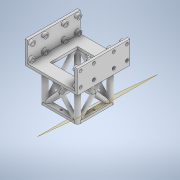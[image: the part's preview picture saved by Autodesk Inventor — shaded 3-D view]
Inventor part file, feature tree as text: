
AUTODESK INVENTOR PART (.ipt)
format: ipt  version: 2022 (Build 260153000, 153)  size: 368,128 bytes
history: native  units: in
note: dims shown in document units (in); Inventor stores cm internally (conversion verified against a paired STEP export)
features: extrude x9, sketch x9, mirror x2, pattern_circular x2, plane x1
ambient origin geometry x8: Origin, YZ Plane, XZ Plane, XY Plane, X Axis, Y Axis, Z Axis, Center Point
bodies: Solid1 (feature_tree)
feature tree (23):
  extrude  "Extrusion1"  Depth=4.0551in
  extrude  "Extrusion2"  Depth=0.1969in
  extrude  "Extrusion3"  Depth=1.5748in TaperAngle=0.0deg
  extrude  "Extrusion4"  Depth=0.3937in
  mirror  "Mirror1"
  extrude  "Extrusion5"  Depth=0.3937in
  extrude  "Extrusion6"  Depth=0.3937in
  extrude  "Extrusion7"  Depth=0.3937in
  extrude  "Extrusion8"  Depth=0.2362in
  pattern_circular  "Circular Pattern1"  [2 undecoded]
  plane  "Work Plane1"
  extrude  "Extrusion9"  Depth=0.3937in
  mirror  "Mirror2"
  pattern_circular  "Circular Pattern2"  [2 undecoded]
  sketch  "Sketch1"  dims[d0=4.0551in d1=4.0551in]
  sketch  "Sketch2"  dims[d2=0.1969in d3=0.0in d4=0.1969in]
  sketch  "Sketch3"  dims[d5=0.1969in d6=1.5748in d7=0.0in]
  sketch  "Sketch4"  dims[d8=0.3937in d9=0.3937in]
  sketch  "Sketch5"  dims[d10=0.3937in d11=0.3937in]
  sketch  "Sketch6"  dims[d12=0.3937in d13=0.3937in]
  sketch  "Sketch7"  dims[d14=0.3937in d15=0.3937in]
  sketch  "Sketch8"  dims[d16=0.2362in d17=0.2362in]
  sketch  "Sketch9"  dims[d18=0.2362in d19=0.2362in d20=0.2362in d21=0.2362in d22=0.2362in d23=0.2362in d24=0.1969in d25=0.0in d26=0.2362in d27=0.2362in d28=0.2362in d29=0.2362in d30=0.2362in d31=0.2362in d32=0.2362in d33=0.2362in d34=0.7874in d35=0.0in d36=0.3937in d37=0.3937in d38=0.3937in d39=0.3937in d40=2.5591in d41=0.0in d42=0.1969in d43=0.0in d44=2.126in d45=2.126in d46=3.937in d47=0.0in d48=0.1575in d49=0.2362in d50=0.0in d51=1.5748in d52=360.0deg d54=0.2886in d55=0.2953in d56=3.2677in d57=0.0in d58=0.0787in d59=0.0in d60=1.5748in d61=360.0deg]
note: 4 required parameter values undecoded (feature->parameter linkage not recoverable at this tier; creation-order binding heuristic only, values carry confidence <= 0.55)
